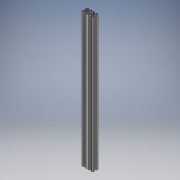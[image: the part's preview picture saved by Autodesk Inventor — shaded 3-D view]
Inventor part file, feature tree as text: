
AUTODESK INVENTOR PART (.ipt)
format: ipt  version: 2018 (Build 220112000, 112)  size: 578,560 bytes
history: native  units: mm
features: other x1, extrude x1, sketch x1
ambient origin geometry x8: Origin, YZ Plane, XZ Plane, XY Plane, X Axis, Y Axis, Z Axis, Center Point
bodies: Body1 (feature_tree)
feature tree (3):
  other  "Sólido1"
  extrude  "Extrusão1"  [1 undecoded]
  sketch  "Esboço1"  dims[d0=725.0mm d1=0.0mm]
note: 1 required parameter value undecoded (feature->parameter linkage not recoverable at this tier; creation-order binding heuristic only, values carry confidence <= 0.55)
